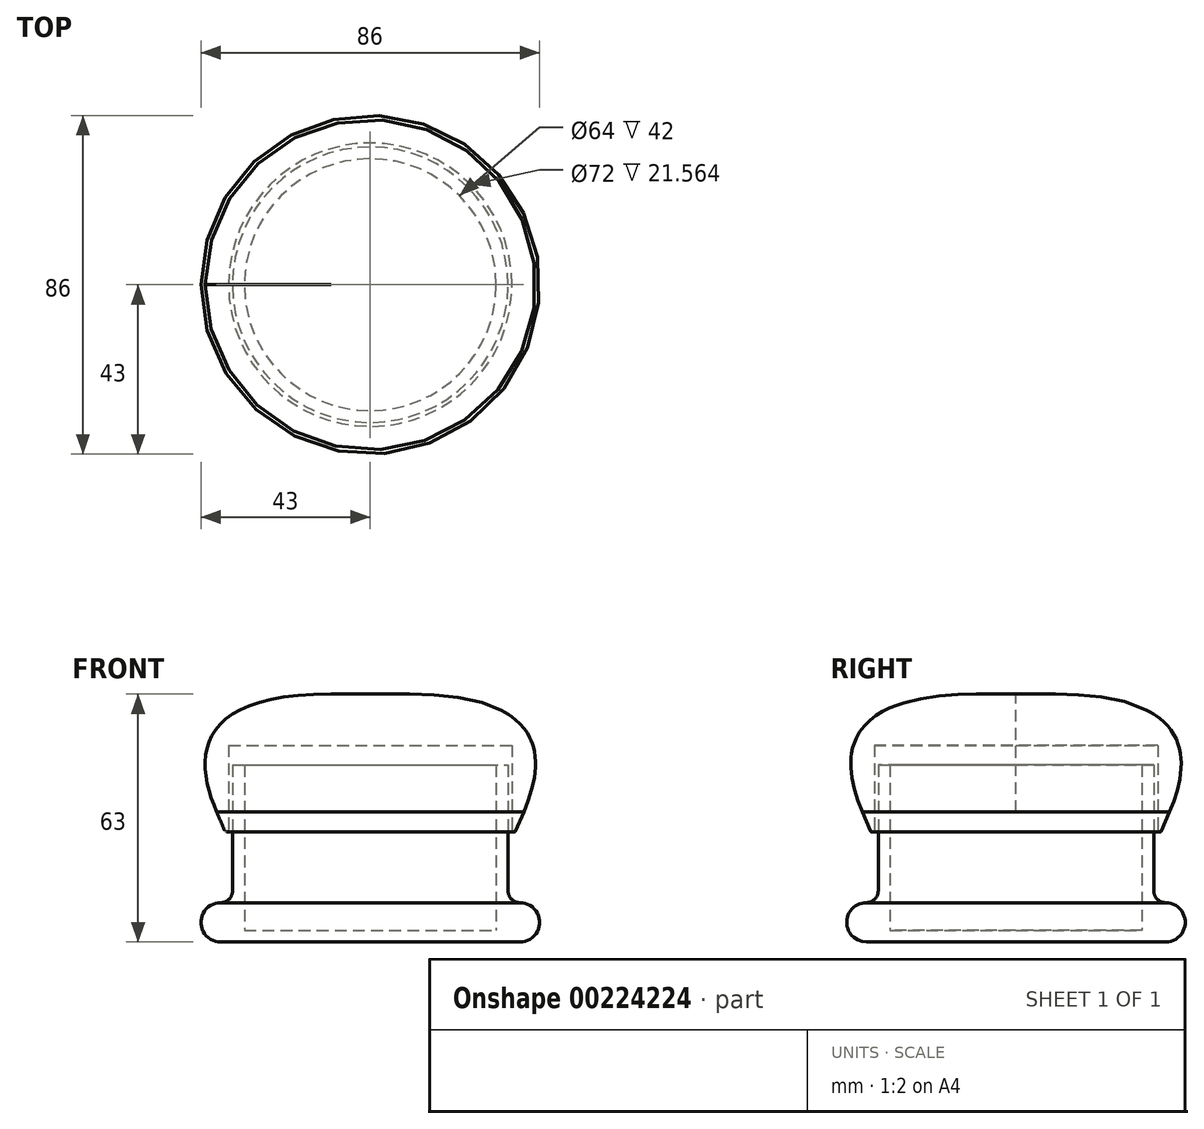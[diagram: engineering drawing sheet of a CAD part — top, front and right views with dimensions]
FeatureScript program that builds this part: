
annotation { "Feature Type Name" : "Feature", "Feature Type Description" : "" }
export const myFeature = defineFeature(function(context is Context, id is Id, definition is map)
    precondition{}
    {
        {
            var Q0;
            Q0=qCreatedBy(makeId("Front.planeOp"),FACE);
            var sketch = newSketch(context, id + "F0", { "sketchPlane" : qUnion([Q0])});
            skLineSegment(sketch, "E0.top", {"start": v(-35, 45) * mm, "end": v(-32, 45) * mm});
            skLineSegment(sketch, "E0.left", {"start": v(-35, 13) * mm, "end": v(-35, 45) * mm});
            skLineSegment(sketch, "E1.top", {"start": v(-32, 3) * mm, "end": v(0, 3) * mm});
            skLineSegment(sketch, "E1.left", {"start": v(-32, 45) * mm, "end": v(-32, 3) * mm});
            skLineSegment(sketch, "E2.top", {"start": v(-36, 50) * mm, "end": v(0, 50) * mm});
            skLineSegment(sketch, "E2.left", {"start": v(-36, 28.44) * mm, "end": v(-36, 50) * mm});
            skLineSegment(sketch, "E3.top", {"start": v(-39, 53) * mm, "end": v(0, 53) * mm});
            skLineSegment(sketch, "E3.left", {"start": v(-39, 33) * mm, "end": v(-39, 53) * mm});
            skLineSegment(sketch, "E4", {"start": v(-36.96, 28.24) * mm, "end": v(-39, 33) * mm});
            skLineSegment(sketch, "E5.bottom", {"start": v(-10, 53) * mm, "end": v(0, 53) * mm});
            skLineSegment(sketch, "E5.top", {"start": v(-10, 63) * mm, "end": v(0, 63) * mm});
            skLineSegment(sketch, "E5.left", {"start": v(-10, 53) * mm, "end": v(-10, 63) * mm});
            skFitSpline(sketch, "E6", {"points": [v(-39, 33) * mm, v(-10, 63) * mm], "startDerivative": vector(-17.73, 41.36) * mm, "endDerivative": vector(105, 0) * mm});
            skLineSegment(sketch, "E7", {"start": v(0, 0) * mm, "end": v(0, 63) * mm, "construction": true});
            skLineSegment(sketch, "E8", {"start": v(0, 0) * mm, "end": v(0, 3) * mm});
            skLineSegment(sketch, "E9", {"start": v(0, 50) * mm, "end": v(0, 53) * mm});
            skLineSegment(sketch, "E10", {"start": v(0, 53) * mm, "end": v(0, 63) * mm});
            skPoint(sketch, "E11.visualSharp", {"position": v(-36, 26) * mm});
            skArc(sketch, "E11.filletArc", {"start": v(-36.96, 28.24) * mm, "mid": v(-36.4, 27.95) * mm, "end": v(-36, 28.44) * mm});
            skLineSegment(sketch, "E12", {"start": v(-38, 0) * mm, "end": v(0, 0) * mm});
            skArc(sketch, "E13", {"start": v(-38, 10) * mm, "mid": v(-43, 5) * mm, "end": v(-38, 0) * mm});
            skArc(sketch, "E14", {"start": v(-38, 10) * mm, "mid": v(-35.88, 10.88) * mm, "end": v(-35, 13) * mm});
            skSolve(sketch);
        }
        {
            var Q0;
            Q0=makeQuery(id+"F0.imprint","IMPRINT",FACE,{"disambiguationData":[TD([[makeQuery(id+"F0.imprint","IMPRINT",EDGE,{"derivedFrom":sQuery(id+"F0.wireOp",EDGE,"E2.top")}),1.0]])]});
            var Q1;
            Q1=makeQuery(id+"F0.imprint","IMPRINT",FACE,{"disambiguationData":[TD([[makeQuery(id+"F0.imprint","IMPRINT",EDGE,{"derivedFrom":sQuery(id+"F0.wireOp",EDGE,"E3.top")}),1.0]])]});
            var Q2;
            Q2=makeQuery(id+"F0.imprint","IMPRINT",FACE,{"disambiguationData":[TD([[makeQuery(id+"F0.imprint","IMPRINT",EDGE,{"derivedFrom":sQuery(id+"F0.wireOp",EDGE,"E5.bottom")}),1.0]])]});
            var Q3;
            Q3=sQuery(id+"F0.wireOp",EDGE,"E7");
            revolve(context, id + "F1", {"entities" : qUnion([Q0, Q1, Q2]), "axis" : qUnion([Q3]), "revolveType" : RevolveType.FULL});
        }
        {
            var Q0;
            Q0=makeQuery(id+"F0.imprint","IMPRINT",FACE,{"disambiguationData":[TD([[makeQuery(id+"F0.imprint","IMPRINT",EDGE,{"derivedFrom":sQuery(id+"F0.wireOp",EDGE,"E0.top")}),-1.0]])]});
            var Q1;
            Q1=sQuery(id+"F0.wireOp",EDGE,"E7");
            revolve(context, id + "F2", {"entities" : qUnion([Q0]), "axis" : qUnion([Q1]), "revolveType" : RevolveType.FULL});
        }
    });
